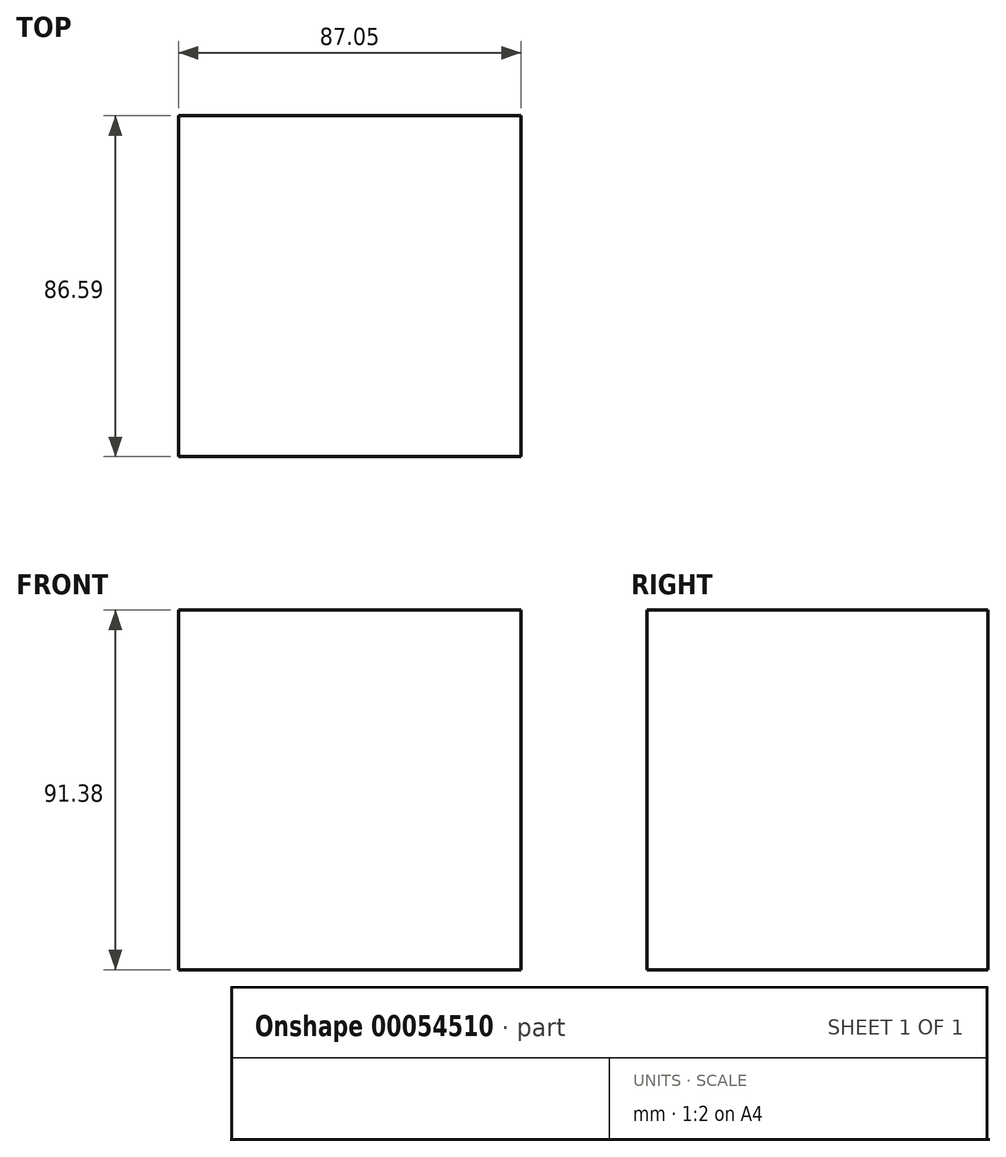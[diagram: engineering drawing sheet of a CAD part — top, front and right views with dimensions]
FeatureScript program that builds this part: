
annotation { "Feature Type Name" : "Feature", "Feature Type Description" : "" }
export const myFeature = defineFeature(function(context is Context, id is Id, definition is map)
    precondition{}
    {
        {
            var Q0;
            Q0=qCreatedBy(makeId("Front.planeOp"),FACE);
            var sketch = newSketch(context, id + "F0", { "sketchPlane" : qUnion([Q0])});
            skLineSegment(sketch, "E0.bottom", {"start": v(-44.6, 48.94) * mm, "end": v(42.44, 48.94) * mm});
            skLineSegment(sketch, "E0.top", {"start": v(-44.6, -42.44) * mm, "end": v(42.44, -42.44) * mm});
            skLineSegment(sketch, "E0.left", {"start": v(-44.6, 48.94) * mm, "end": v(-44.6, -42.44) * mm});
            skLineSegment(sketch, "E0.right", {"start": v(42.44, 48.94) * mm, "end": v(42.44, -42.44) * mm});
            skSolve(sketch);
        }
        {
            var Q0;
            Q0=makeQuery(id+"F0.imprint","IMPRINT",FACE,{"disambiguationData":[TD([[makeQuery(id+"F0.imprint","IMPRINT",EDGE,{"derivedFrom":sQuery(id+"F0.wireOp",EDGE,"E0.bottom")}),-1.0]])]});
            extrude(context, id + "F1", {"entities" : qUnion([Q0]), "depth" : 86.6 * mm});
        }
    });
